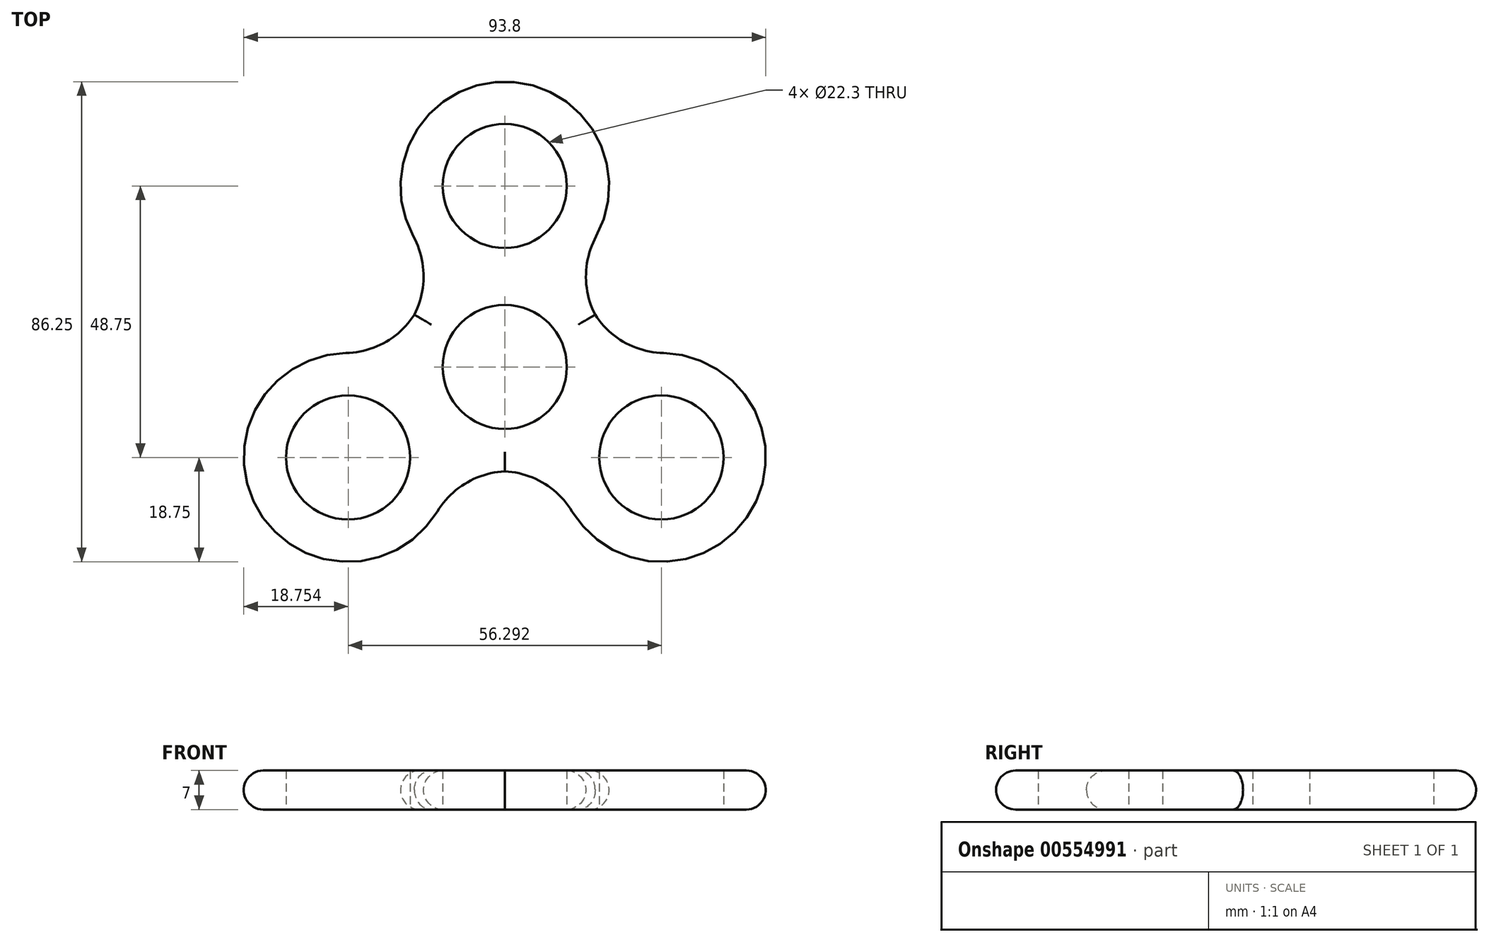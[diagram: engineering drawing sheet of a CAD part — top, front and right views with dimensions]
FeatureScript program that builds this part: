
annotation { "Feature Type Name" : "Feature", "Feature Type Description" : "" }
export const myFeature = defineFeature(function(context is Context, id is Id, definition is map)
    precondition{}
    {
        {
            var Q0;
            Q0=qCreatedBy(makeId("Top.planeOp"),FACE);
            var sketch = newSketch(context, id + "F0", { "sketchPlane" : qUnion([Q0])});
            skCircle(sketch, "E0", {"center": v(0, 0) * mm, "radius": 11.15 * mm});
            skLineSegment(sketch, "E1", {"start": v(0, 0) * mm, "end": v(0, 32.5) * mm, "construction": true});
            skCircle(sketch, "E2", {"center": v(0, 32.5) * mm, "radius": 11.15 * mm});
            skCircle(sketch, "E3.1.0", {"center": v(-28.15, -16.25) * mm, "radius": 11.15 * mm});
            skCircle(sketch, "E3.2.0", {"center": v(28.15, -16.25) * mm, "radius": 11.15 * mm});
            skCircle(sketch, "E4", {"center": v(0, 32.5) * mm, "radius": 18.75 * mm});
            skCircle(sketch, "E5", {"center": v(28.15, -16.25) * mm, "radius": 18.75 * mm});
            skCircle(sketch, "E6", {"center": v(-28.15, -16.25) * mm, "radius": 18.75 * mm});
            skLineSegment(sketch, "E7", {"start": v(0, 0) * mm, "end": v(-28.15, -16.25) * mm});
            skCircle(sketch, "E8", {"center": v(0, 0) * mm, "radius": 18.75 * mm});
            skSolve(sketch);
        }
        {
            var Q0;
            Q0 = qSketchRegion(id + "F0", true);
            extrude(context, id + "F1", {"entities" : qUnion([Q0]), "depth" : 7 * mm, "offsetDistance" : 25 * mm});
        }
        {
            var Q0;
            {var subQ0=sQuery(id+"F0.wireOp",EDGE,"E8");var subQ1=sQuery(id+"F0.wireOp",EDGE,"E6");Q0=makeQuery(id+"F1.opExtrude","SWEPT_EDGE",EDGE,{"disambiguationData":[OSD([subQ1,subQ0]),TDD([makeQuery(id+"F0.imprint","INTERSECT",VERTEX,{"disambiguationData":[OD(1.0)],"derivedFrom":[subQ1,subQ0]})])]});}
            var Q1;
            {var subQ0=sQuery(id+"F0.wireOp",EDGE,"E8");var subQ1=sQuery(id+"F0.wireOp",EDGE,"E4");Q1=makeQuery(id+"F1.opExtrude","SWEPT_EDGE",EDGE,{"disambiguationData":[OSD([subQ1,subQ0]),TDD([makeQuery(id+"F0.imprint","INTERSECT",VERTEX,{"disambiguationData":[OD(0.0)],"derivedFrom":[subQ1,subQ0]})])]});}
            var Q2;
            {var subQ0=sQuery(id+"F0.wireOp",EDGE,"E8");var subQ1=sQuery(id+"F0.wireOp",EDGE,"E4");Q2=makeQuery(id+"F1.opExtrude","SWEPT_EDGE",EDGE,{"disambiguationData":[OSD([subQ1,subQ0]),TDD([makeQuery(id+"F0.imprint","INTERSECT",VERTEX,{"disambiguationData":[OD(1.0)],"derivedFrom":[subQ1,subQ0]})])]});}
            var Q3;
            {var subQ0=sQuery(id+"F0.wireOp",EDGE,"E8");var subQ1=sQuery(id+"F0.wireOp",EDGE,"E5");Q3=makeQuery(id+"F1.opExtrude","SWEPT_EDGE",EDGE,{"disambiguationData":[OSD([subQ1,subQ0]),TDD([makeQuery(id+"F0.imprint","INTERSECT",VERTEX,{"disambiguationData":[OD(1.0)],"derivedFrom":[subQ1,subQ0]})])]});}
            var Q4;
            {var subQ0=sQuery(id+"F0.wireOp",EDGE,"E8");var subQ1=sQuery(id+"F0.wireOp",EDGE,"E5");Q4=makeQuery(id+"F1.opExtrude","SWEPT_EDGE",EDGE,{"disambiguationData":[OSD([subQ1,subQ0]),TDD([makeQuery(id+"F0.imprint","INTERSECT",VERTEX,{"disambiguationData":[OD(0.0)],"derivedFrom":[subQ1,subQ0]})])]});}
            var Q5;
            {var subQ0=sQuery(id+"F0.wireOp",EDGE,"E8");var subQ1=sQuery(id+"F0.wireOp",EDGE,"E6");Q5=makeQuery(id+"F1.opExtrude","SWEPT_EDGE",EDGE,{"disambiguationData":[OSD([subQ1,subQ0]),TDD([makeQuery(id+"F0.imprint","INTERSECT",VERTEX,{"disambiguationData":[OD(0.0)],"derivedFrom":[subQ1,subQ0]})])]});}
            fillet(context, id + "F2", {"entities" : qUnion([Q0, Q1, Q2, Q3, Q4, Q5]), "radius" : 15 * mm, "tangentPropagation" : true, "allowEdgeOverflow" : false});
        }
        {
            var Q0;
            Q0=makeQuery(id+"F1.opExtrude","CAP_EDGE",EDGE,{"disambiguationData":[OSD([sQuery(id+"F0.wireOp",EDGE,"E4")])],"isStart":false});
            var Q1;
            {var subQ0=sQuery(id+"F0.wireOp",EDGE,"E8");var subQ1=sQuery(id+"F0.wireOp",EDGE,"E4");Q1=makeQuery(id+"F2.opFillet","BLEND_EDGE",EDGE,{"blendedFrom":[makeQuery(id+"F1.opExtrude","SWEPT_EDGE",EDGE,{"disambiguationData":[OSD([subQ1,subQ0]),TDD([makeQuery(id+"F0.imprint","INTERSECT",VERTEX,{"disambiguationData":[OD(0.0)],"derivedFrom":[subQ1,subQ0]})])]}),makeQuery(id+"F1.opExtrude","CAP_FACE",FACE,{"disambiguationData":[OSD([sQuery(id+"F0.wireOp",EDGE,"E0"),sQuery(id+"F0.wireOp",EDGE,"E2"),sQuery(id+"F0.wireOp",EDGE,"E3.1.0"),sQuery(id+"F0.wireOp",EDGE,"E3.2.0"),subQ1,sQuery(id+"F0.wireOp",EDGE,"E5"),sQuery(id+"F0.wireOp",EDGE,"E6"),subQ0])],"isStart":false})],"blendedInto":[makeQuery(id+"F1.opExtrude","CAP_FACE",FACE,{"disambiguationData":[OSD([sQuery(id+"F0.wireOp",EDGE,"E0"),sQuery(id+"F0.wireOp",EDGE,"E2"),sQuery(id+"F0.wireOp",EDGE,"E3.1.0"),sQuery(id+"F0.wireOp",EDGE,"E3.2.0"),subQ1,sQuery(id+"F0.wireOp",EDGE,"E5"),sQuery(id+"F0.wireOp",EDGE,"E6"),subQ0])],"isStart":false})]});}
            var Q2;
            {var subQ0=sQuery(id+"F0.wireOp",EDGE,"E8");var subQ1=sQuery(id+"F0.wireOp",EDGE,"E6");Q2=makeQuery(id+"F2.opFillet","BLEND_EDGE",EDGE,{"blendedFrom":[makeQuery(id+"F1.opExtrude","SWEPT_EDGE",EDGE,{"disambiguationData":[OSD([subQ1,subQ0]),TDD([makeQuery(id+"F0.imprint","INTERSECT",VERTEX,{"disambiguationData":[OD(1.0)],"derivedFrom":[subQ1,subQ0]})])]}),makeQuery(id+"F1.opExtrude","CAP_FACE",FACE,{"disambiguationData":[OSD([sQuery(id+"F0.wireOp",EDGE,"E0"),sQuery(id+"F0.wireOp",EDGE,"E2"),sQuery(id+"F0.wireOp",EDGE,"E3.1.0"),sQuery(id+"F0.wireOp",EDGE,"E3.2.0"),sQuery(id+"F0.wireOp",EDGE,"E4"),sQuery(id+"F0.wireOp",EDGE,"E5"),subQ1,subQ0])],"isStart":false})],"blendedInto":[makeQuery(id+"F1.opExtrude","CAP_FACE",FACE,{"disambiguationData":[OSD([sQuery(id+"F0.wireOp",EDGE,"E0"),sQuery(id+"F0.wireOp",EDGE,"E2"),sQuery(id+"F0.wireOp",EDGE,"E3.1.0"),sQuery(id+"F0.wireOp",EDGE,"E3.2.0"),sQuery(id+"F0.wireOp",EDGE,"E4"),sQuery(id+"F0.wireOp",EDGE,"E5"),subQ1,subQ0])],"isStart":false})]});}
            var Q3;
            Q3=makeQuery(id+"F1.opExtrude","CAP_EDGE",EDGE,{"disambiguationData":[OSD([sQuery(id+"F0.wireOp",EDGE,"E6")])],"isStart":false});
            var Q4;
            {var subQ0=sQuery(id+"F0.wireOp",EDGE,"E8");var subQ1=sQuery(id+"F0.wireOp",EDGE,"E5");Q4=makeQuery(id+"F2.opFillet","BLEND_EDGE",EDGE,{"blendedFrom":[makeQuery(id+"F1.opExtrude","SWEPT_EDGE",EDGE,{"disambiguationData":[OSD([subQ1,subQ0]),TDD([makeQuery(id+"F0.imprint","INTERSECT",VERTEX,{"disambiguationData":[OD(0.0)],"derivedFrom":[subQ1,subQ0]})])]}),makeQuery(id+"F1.opExtrude","CAP_FACE",FACE,{"disambiguationData":[OSD([sQuery(id+"F0.wireOp",EDGE,"E0"),sQuery(id+"F0.wireOp",EDGE,"E2"),sQuery(id+"F0.wireOp",EDGE,"E3.1.0"),sQuery(id+"F0.wireOp",EDGE,"E3.2.0"),sQuery(id+"F0.wireOp",EDGE,"E4"),subQ1,sQuery(id+"F0.wireOp",EDGE,"E6"),subQ0])],"isStart":false})],"blendedInto":[makeQuery(id+"F1.opExtrude","CAP_FACE",FACE,{"disambiguationData":[OSD([sQuery(id+"F0.wireOp",EDGE,"E0"),sQuery(id+"F0.wireOp",EDGE,"E2"),sQuery(id+"F0.wireOp",EDGE,"E3.1.0"),sQuery(id+"F0.wireOp",EDGE,"E3.2.0"),sQuery(id+"F0.wireOp",EDGE,"E4"),subQ1,sQuery(id+"F0.wireOp",EDGE,"E6"),subQ0])],"isStart":false})]});}
            var Q5;
            Q5=makeQuery(id+"F1.opExtrude","CAP_EDGE",EDGE,{"disambiguationData":[OSD([sQuery(id+"F0.wireOp",EDGE,"E5")])],"isStart":false});
            var Q6;
            Q6=makeQuery(id+"F1.opExtrude","CAP_EDGE",EDGE,{"disambiguationData":[OSD([sQuery(id+"F0.wireOp",EDGE,"E6")])],"isStart":true});
            var Q7;
            {var subQ0=sQuery(id+"F0.wireOp",EDGE,"E8");var subQ1=sQuery(id+"F0.wireOp",EDGE,"E6");Q7=makeQuery(id+"F2.opFillet","BLEND_EDGE",EDGE,{"blendedFrom":[makeQuery(id+"F1.opExtrude","SWEPT_EDGE",EDGE,{"disambiguationData":[OSD([subQ1,subQ0]),TDD([makeQuery(id+"F0.imprint","INTERSECT",VERTEX,{"disambiguationData":[OD(0.0)],"derivedFrom":[subQ1,subQ0]})])]}),makeQuery(id+"F1.opExtrude","CAP_FACE",FACE,{"disambiguationData":[OSD([sQuery(id+"F0.wireOp",EDGE,"E0"),sQuery(id+"F0.wireOp",EDGE,"E2"),sQuery(id+"F0.wireOp",EDGE,"E3.1.0"),sQuery(id+"F0.wireOp",EDGE,"E3.2.0"),sQuery(id+"F0.wireOp",EDGE,"E4"),sQuery(id+"F0.wireOp",EDGE,"E5"),subQ1,subQ0])],"isStart":true})],"blendedInto":[makeQuery(id+"F1.opExtrude","CAP_FACE",FACE,{"disambiguationData":[OSD([sQuery(id+"F0.wireOp",EDGE,"E0"),sQuery(id+"F0.wireOp",EDGE,"E2"),sQuery(id+"F0.wireOp",EDGE,"E3.1.0"),sQuery(id+"F0.wireOp",EDGE,"E3.2.0"),sQuery(id+"F0.wireOp",EDGE,"E4"),sQuery(id+"F0.wireOp",EDGE,"E5"),subQ1,subQ0])],"isStart":true})]});}
            var Q8;
            Q8=makeQuery(id+"F1.opExtrude","CAP_EDGE",EDGE,{"disambiguationData":[OSD([sQuery(id+"F0.wireOp",EDGE,"E5")])],"isStart":true});
            var Q9;
            {var subQ0=sQuery(id+"F0.wireOp",EDGE,"E8");var subQ1=sQuery(id+"F0.wireOp",EDGE,"E5");Q9=makeQuery(id+"F2.opFillet","BLEND_EDGE",EDGE,{"blendedFrom":[makeQuery(id+"F1.opExtrude","SWEPT_EDGE",EDGE,{"disambiguationData":[OSD([subQ1,subQ0]),TDD([makeQuery(id+"F0.imprint","INTERSECT",VERTEX,{"disambiguationData":[OD(1.0)],"derivedFrom":[subQ1,subQ0]})])]}),makeQuery(id+"F1.opExtrude","CAP_FACE",FACE,{"disambiguationData":[OSD([sQuery(id+"F0.wireOp",EDGE,"E0"),sQuery(id+"F0.wireOp",EDGE,"E2"),sQuery(id+"F0.wireOp",EDGE,"E3.1.0"),sQuery(id+"F0.wireOp",EDGE,"E3.2.0"),sQuery(id+"F0.wireOp",EDGE,"E4"),subQ1,sQuery(id+"F0.wireOp",EDGE,"E6"),subQ0])],"isStart":true})],"blendedInto":[makeQuery(id+"F1.opExtrude","CAP_FACE",FACE,{"disambiguationData":[OSD([sQuery(id+"F0.wireOp",EDGE,"E0"),sQuery(id+"F0.wireOp",EDGE,"E2"),sQuery(id+"F0.wireOp",EDGE,"E3.1.0"),sQuery(id+"F0.wireOp",EDGE,"E3.2.0"),sQuery(id+"F0.wireOp",EDGE,"E4"),subQ1,sQuery(id+"F0.wireOp",EDGE,"E6"),subQ0])],"isStart":true})]});}
            var Q10;
            {var subQ0=sQuery(id+"F0.wireOp",EDGE,"E8");var subQ1=sQuery(id+"F0.wireOp",EDGE,"E4");Q10=makeQuery(id+"F2.opFillet","BLEND_EDGE",EDGE,{"blendedFrom":[makeQuery(id+"F1.opExtrude","SWEPT_EDGE",EDGE,{"disambiguationData":[OSD([subQ1,subQ0]),TDD([makeQuery(id+"F0.imprint","INTERSECT",VERTEX,{"disambiguationData":[OD(1.0)],"derivedFrom":[subQ1,subQ0]})])]}),makeQuery(id+"F1.opExtrude","CAP_FACE",FACE,{"disambiguationData":[OSD([sQuery(id+"F0.wireOp",EDGE,"E0"),sQuery(id+"F0.wireOp",EDGE,"E2"),sQuery(id+"F0.wireOp",EDGE,"E3.1.0"),sQuery(id+"F0.wireOp",EDGE,"E3.2.0"),subQ1,sQuery(id+"F0.wireOp",EDGE,"E5"),sQuery(id+"F0.wireOp",EDGE,"E6"),subQ0])],"isStart":true})],"blendedInto":[makeQuery(id+"F1.opExtrude","CAP_FACE",FACE,{"disambiguationData":[OSD([sQuery(id+"F0.wireOp",EDGE,"E0"),sQuery(id+"F0.wireOp",EDGE,"E2"),sQuery(id+"F0.wireOp",EDGE,"E3.1.0"),sQuery(id+"F0.wireOp",EDGE,"E3.2.0"),subQ1,sQuery(id+"F0.wireOp",EDGE,"E5"),sQuery(id+"F0.wireOp",EDGE,"E6"),subQ0])],"isStart":true})]});}
            var Q11;
            Q11=makeQuery(id+"F1.opExtrude","CAP_EDGE",EDGE,{"disambiguationData":[OSD([sQuery(id+"F0.wireOp",EDGE,"E4")])],"isStart":true});
            fillet(context, id + "F3", {"entities" : qUnion([Q0, Q1, Q2, Q3, Q4, Q5, Q6, Q7, Q8, Q9, Q10, Q11]), "radius" : 3.5 * mm, "tangentPropagation" : true, "allowEdgeOverflow" : false});
        }
    });
